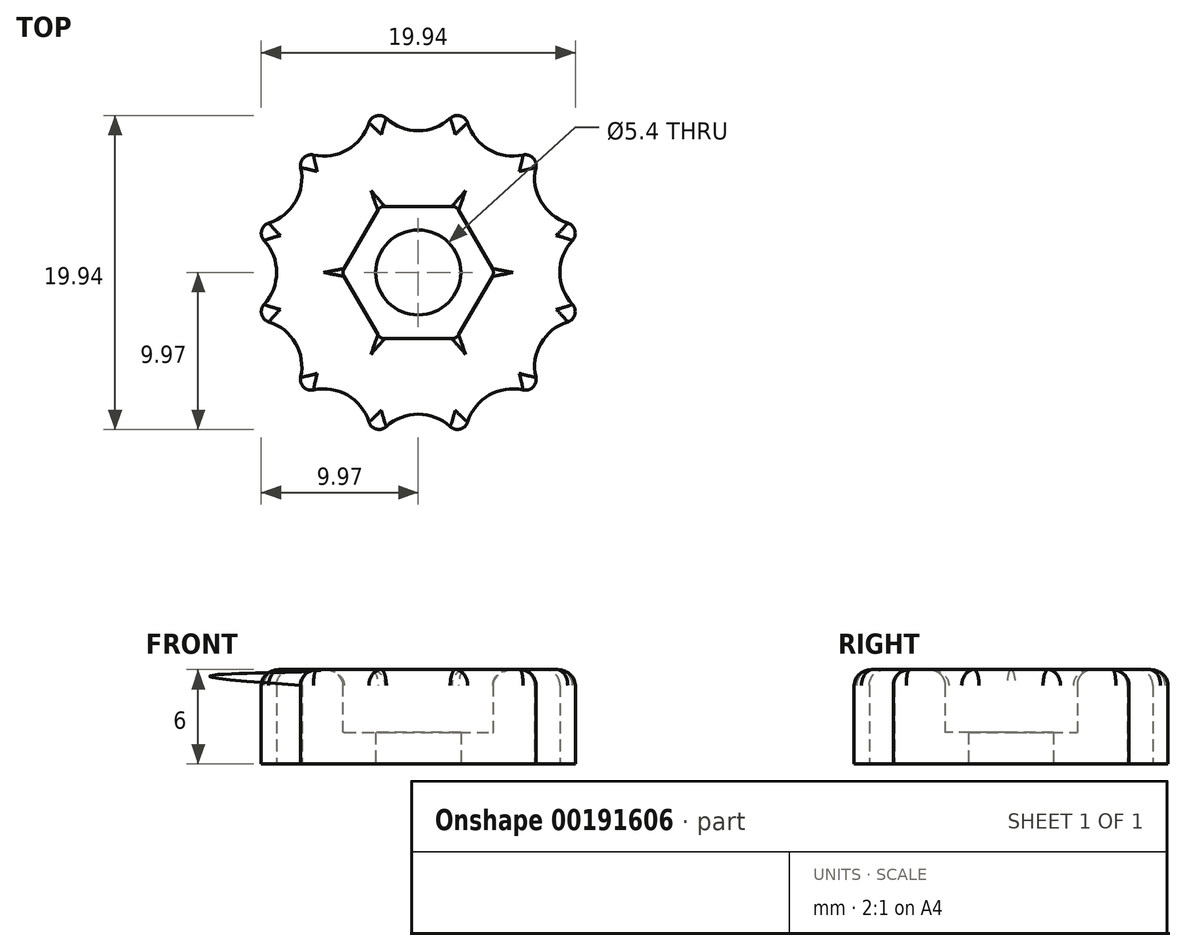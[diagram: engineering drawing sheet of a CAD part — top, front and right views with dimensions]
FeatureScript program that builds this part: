
annotation { "Feature Type Name" : "Feature", "Feature Type Description" : "" }
export const myFeature = defineFeature(function(context is Context, id is Id, definition is map)
    precondition{}
    {
        {
            var Q0;
            Q0=qCreatedBy(makeId("Top.planeOp"),FACE);
            var sketch = newSketch(context, id + "F0", { "sketchPlane" : qUnion([Q0])});
            skCircle(sketch, "E0.cCircle", {"center": v(0, 0) * mm, "radius": 4.2 * mm, "construction": true});
            skLineSegment(sketch, "E0.0", {"start": v(-2.42, 4.2) * mm, "end": v(2.42, 4.2) * mm});
            skLineSegment(sketch, "E0.1", {"start": v(2.42, 4.2) * mm, "end": v(4.85, 0) * mm});
            skLineSegment(sketch, "E0.2", {"start": v(4.85, 0) * mm, "end": v(2.42, -4.2) * mm});
            skLineSegment(sketch, "E0.3", {"start": v(2.42, -4.2) * mm, "end": v(-2.42, -4.2) * mm});
            skLineSegment(sketch, "E0.4", {"start": v(-2.42, -4.2) * mm, "end": v(-4.85, 0) * mm});
            skLineSegment(sketch, "E0.5", {"start": v(-4.85, 0) * mm, "end": v(-2.42, 4.2) * mm});
            skPoint(sketch, "E0.0.midPoint", {"position": v(0, 4.2) * mm});
            skCircle(sketch, "E1", {"center": v(0, 0) * mm, "radius": 2.7 * mm});
            skArc(sketch, "E2", {"start": v(-2.03, 9.8) * mm, "mid": v(0, 9) * mm, "end": v(2.03, 9.8) * mm});
            skArc(sketch, "E3.1.0", {"start": v(-6.65, 7.46) * mm, "mid": v(-4.5, 7.8) * mm, "end": v(-3.14, 9.5) * mm});
            skArc(sketch, "E3.2.0", {"start": v(-9.5, 3.14) * mm, "mid": v(-7.8, 4.5) * mm, "end": v(-7.46, 6.65) * mm});
            skArc(sketch, "E3.3.0", {"start": v(-9.8, -2.03) * mm, "mid": v(-9, 0) * mm, "end": v(-9.8, 2.03) * mm});
            skArc(sketch, "E3.4.0", {"start": v(-7.46, -6.65) * mm, "mid": v(-7.8, -4.5) * mm, "end": v(-9.5, -3.14) * mm});
            skArc(sketch, "E3.5.0", {"start": v(-3.14, -9.5) * mm, "mid": v(-4.5, -7.8) * mm, "end": v(-6.65, -7.46) * mm});
            skArc(sketch, "E3.6.0", {"start": v(2.03, -9.8) * mm, "mid": v(0, -9) * mm, "end": v(-2.03, -9.8) * mm});
            skArc(sketch, "E3.7.0", {"start": v(6.65, -7.46) * mm, "mid": v(4.5, -7.8) * mm, "end": v(3.14, -9.5) * mm});
            skArc(sketch, "E3.8.0", {"start": v(9.5, -3.14) * mm, "mid": v(7.8, -4.5) * mm, "end": v(7.46, -6.65) * mm});
            skArc(sketch, "E3.9.0", {"start": v(9.8, 2.03) * mm, "mid": v(9, 0) * mm, "end": v(9.8, -2.03) * mm});
            skArc(sketch, "E3.10.0", {"start": v(7.46, 6.65) * mm, "mid": v(7.8, 4.5) * mm, "end": v(9.5, 3.14) * mm});
            skArc(sketch, "E3.11.0", {"start": v(3.14, 9.5) * mm, "mid": v(4.5, 7.8) * mm, "end": v(6.65, 7.46) * mm});
            skArc(sketch, "E4", {"start": v(-3.14, 9.5) * mm, "mid": v(-2.67, 9.95) * mm, "end": v(-2.03, 9.8) * mm});
            skArc(sketch, "E5.1.0", {"start": v(-7.46, 6.65) * mm, "mid": v(-7.28, 7.28) * mm, "end": v(-6.65, 7.46) * mm});
            skArc(sketch, "E5.2.0", {"start": v(-9.8, 2.03) * mm, "mid": v(-9.95, 2.67) * mm, "end": v(-9.5, 3.14) * mm});
            skArc(sketch, "E5.3.0", {"start": v(-9.5, -3.14) * mm, "mid": v(-9.95, -2.67) * mm, "end": v(-9.8, -2.03) * mm});
            skArc(sketch, "E5.4.0", {"start": v(-6.65, -7.46) * mm, "mid": v(-7.28, -7.28) * mm, "end": v(-7.46, -6.65) * mm});
            skArc(sketch, "E5.5.0", {"start": v(-2.03, -9.8) * mm, "mid": v(-2.67, -9.95) * mm, "end": v(-3.14, -9.5) * mm});
            skArc(sketch, "E5.6.0", {"start": v(3.14, -9.5) * mm, "mid": v(2.67, -9.95) * mm, "end": v(2.03, -9.8) * mm});
            skArc(sketch, "E5.7.0", {"start": v(7.46, -6.65) * mm, "mid": v(7.28, -7.28) * mm, "end": v(6.65, -7.46) * mm});
            skArc(sketch, "E5.8.0", {"start": v(9.8, -2.03) * mm, "mid": v(9.95, -2.67) * mm, "end": v(9.5, -3.14) * mm});
            skArc(sketch, "E5.9.0", {"start": v(9.5, 3.14) * mm, "mid": v(9.95, 2.67) * mm, "end": v(9.8, 2.03) * mm});
            skArc(sketch, "E5.10.0", {"start": v(6.65, 7.46) * mm, "mid": v(7.28, 7.28) * mm, "end": v(7.46, 6.65) * mm});
            skArc(sketch, "E5.11.0", {"start": v(2.03, 9.8) * mm, "mid": v(2.67, 9.95) * mm, "end": v(3.14, 9.5) * mm});
            skSolve(sketch);
        }
        {
            var Q0;
            Q0=makeQuery(id+"F0.imprint","IMPRINT",FACE,{"disambiguationData":[TD([[makeQuery(id+"F0.imprint","IMPRINT",EDGE,{"derivedFrom":sQuery(id+"F0.wireOp",EDGE,"E0.0")}),1.0]])]});
            extrude(context, id + "F1", {"entities" : qUnion([Q0]), "depth" : 6 * mm});
        }
        {
            var Q0;
            Q0=makeQuery(id+"F1.opExtrude","CAP_FACE",FACE,{"disambiguationData":[OSD([sQuery(id+"F0.wireOp",EDGE,"E0.0"),sQuery(id+"F0.wireOp",EDGE,"E0.1"),sQuery(id+"F0.wireOp",EDGE,"E0.2"),sQuery(id+"F0.wireOp",EDGE,"E0.3"),sQuery(id+"F0.wireOp",EDGE,"E0.4"),sQuery(id+"F0.wireOp",EDGE,"E0.5"),sQuery(id+"F0.wireOp",EDGE,"E2"),sQuery(id+"F0.wireOp",EDGE,"E3.1.0"),sQuery(id+"F0.wireOp",EDGE,"E3.2.0"),sQuery(id+"F0.wireOp",EDGE,"E3.3.0"),sQuery(id+"F0.wireOp",EDGE,"E3.4.0"),sQuery(id+"F0.wireOp",EDGE,"E3.5.0"),sQuery(id+"F0.wireOp",EDGE,"E3.6.0"),sQuery(id+"F0.wireOp",EDGE,"E3.7.0"),sQuery(id+"F0.wireOp",EDGE,"E3.8.0"),sQuery(id+"F0.wireOp",EDGE,"E3.9.0"),sQuery(id+"F0.wireOp",EDGE,"E3.10.0"),sQuery(id+"F0.wireOp",EDGE,"E3.11.0"),sQuery(id+"F0.wireOp",EDGE,"E4"),sQuery(id+"F0.wireOp",EDGE,"E5.1.0"),sQuery(id+"F0.wireOp",EDGE,"E5.2.0"),sQuery(id+"F0.wireOp",EDGE,"E5.3.0"),sQuery(id+"F0.wireOp",EDGE,"E5.4.0"),sQuery(id+"F0.wireOp",EDGE,"E5.5.0"),sQuery(id+"F0.wireOp",EDGE,"E5.6.0"),sQuery(id+"F0.wireOp",EDGE,"E5.7.0"),sQuery(id+"F0.wireOp",EDGE,"E5.8.0"),sQuery(id+"F0.wireOp",EDGE,"E5.9.0"),sQuery(id+"F0.wireOp",EDGE,"E5.10.0"),sQuery(id+"F0.wireOp",EDGE,"E5.11.0")])],"isStart":false});
            fillet(context, id + "F2", {"entities" : qUnion([Q0]), "radius" : 1 * mm, "tangentPropagation" : true, "allowEdgeOverflow" : false});
        }
        {
            var Q0;
            Q0=makeQuery(id+"F0.imprint","IMPRINT",FACE,{"disambiguationData":[TD([[makeQuery(id+"F0.imprint","IMPRINT",EDGE,{"derivedFrom":sQuery(id+"F0.wireOp",EDGE,"E0.0")}),-1.0]])]});
            extrude(context, id + "F3", {"entities" : qUnion([Q0]), "operationType" : NewBodyOperationType.ADD, "depth" : 2 * mm});
        }
        {
            var Q0;
            Q0=makeQuery(id+"F2.opFillet","BLEND_EDGE",EDGE,{"blendedFrom":[makeQuery(id+"F1.opExtrude","CAP_EDGE",EDGE,{"disambiguationData":[OSD([sQuery(id+"F0.wireOp",EDGE,"E0.0")])],"isStart":false}),makeQuery(id+"F1.opExtrude","CAP_EDGE",EDGE,{"disambiguationData":[OSD([sQuery(id+"F0.wireOp",EDGE,"E0.5")])],"isStart":false})],"blendedInto":[]});
            var Q1;
            Q1=makeQuery(id+"F2.opFillet","BLEND_EDGE",EDGE,{"blendedFrom":[makeQuery(id+"F1.opExtrude","CAP_EDGE",EDGE,{"disambiguationData":[OSD([sQuery(id+"F0.wireOp",EDGE,"E0.0")])],"isStart":false}),makeQuery(id+"F1.opExtrude","CAP_EDGE",EDGE,{"disambiguationData":[OSD([sQuery(id+"F0.wireOp",EDGE,"E0.1")])],"isStart":false})],"blendedInto":[]});
            var Q2;
            Q2=makeQuery(id+"F2.opFillet","BLEND_EDGE",EDGE,{"blendedFrom":[makeQuery(id+"F1.opExtrude","CAP_EDGE",EDGE,{"disambiguationData":[OSD([sQuery(id+"F0.wireOp",EDGE,"E0.1")])],"isStart":false}),makeQuery(id+"F1.opExtrude","CAP_EDGE",EDGE,{"disambiguationData":[OSD([sQuery(id+"F0.wireOp",EDGE,"E0.2")])],"isStart":false})],"blendedInto":[]});
            var Q3;
            Q3=makeQuery(id+"F2.opFillet","BLEND_EDGE",EDGE,{"blendedFrom":[makeQuery(id+"F1.opExtrude","CAP_EDGE",EDGE,{"disambiguationData":[OSD([sQuery(id+"F0.wireOp",EDGE,"E0.2")])],"isStart":false}),makeQuery(id+"F1.opExtrude","CAP_EDGE",EDGE,{"disambiguationData":[OSD([sQuery(id+"F0.wireOp",EDGE,"E0.3")])],"isStart":false})],"blendedInto":[]});
            var Q4;
            Q4=makeQuery(id+"F2.opFillet","BLEND_EDGE",EDGE,{"blendedFrom":[makeQuery(id+"F1.opExtrude","CAP_EDGE",EDGE,{"disambiguationData":[OSD([sQuery(id+"F0.wireOp",EDGE,"E0.3")])],"isStart":false}),makeQuery(id+"F1.opExtrude","CAP_EDGE",EDGE,{"disambiguationData":[OSD([sQuery(id+"F0.wireOp",EDGE,"E0.4")])],"isStart":false})],"blendedInto":[]});
            var Q5;
            Q5=makeQuery(id+"F2.opFillet","BLEND_EDGE",EDGE,{"blendedFrom":[makeQuery(id+"F1.opExtrude","CAP_EDGE",EDGE,{"disambiguationData":[OSD([sQuery(id+"F0.wireOp",EDGE,"E0.4")])],"isStart":false}),makeQuery(id+"F1.opExtrude","CAP_EDGE",EDGE,{"disambiguationData":[OSD([sQuery(id+"F0.wireOp",EDGE,"E0.5")])],"isStart":false})],"blendedInto":[]});
            fillet(context, id + "F4", {"entities" : qUnion([Q0, Q1, Q2, Q3, Q4, Q5]), "radius" : 0.5 * mm, "tangentPropagation" : true, "allowEdgeOverflow" : false});
        }
    });
